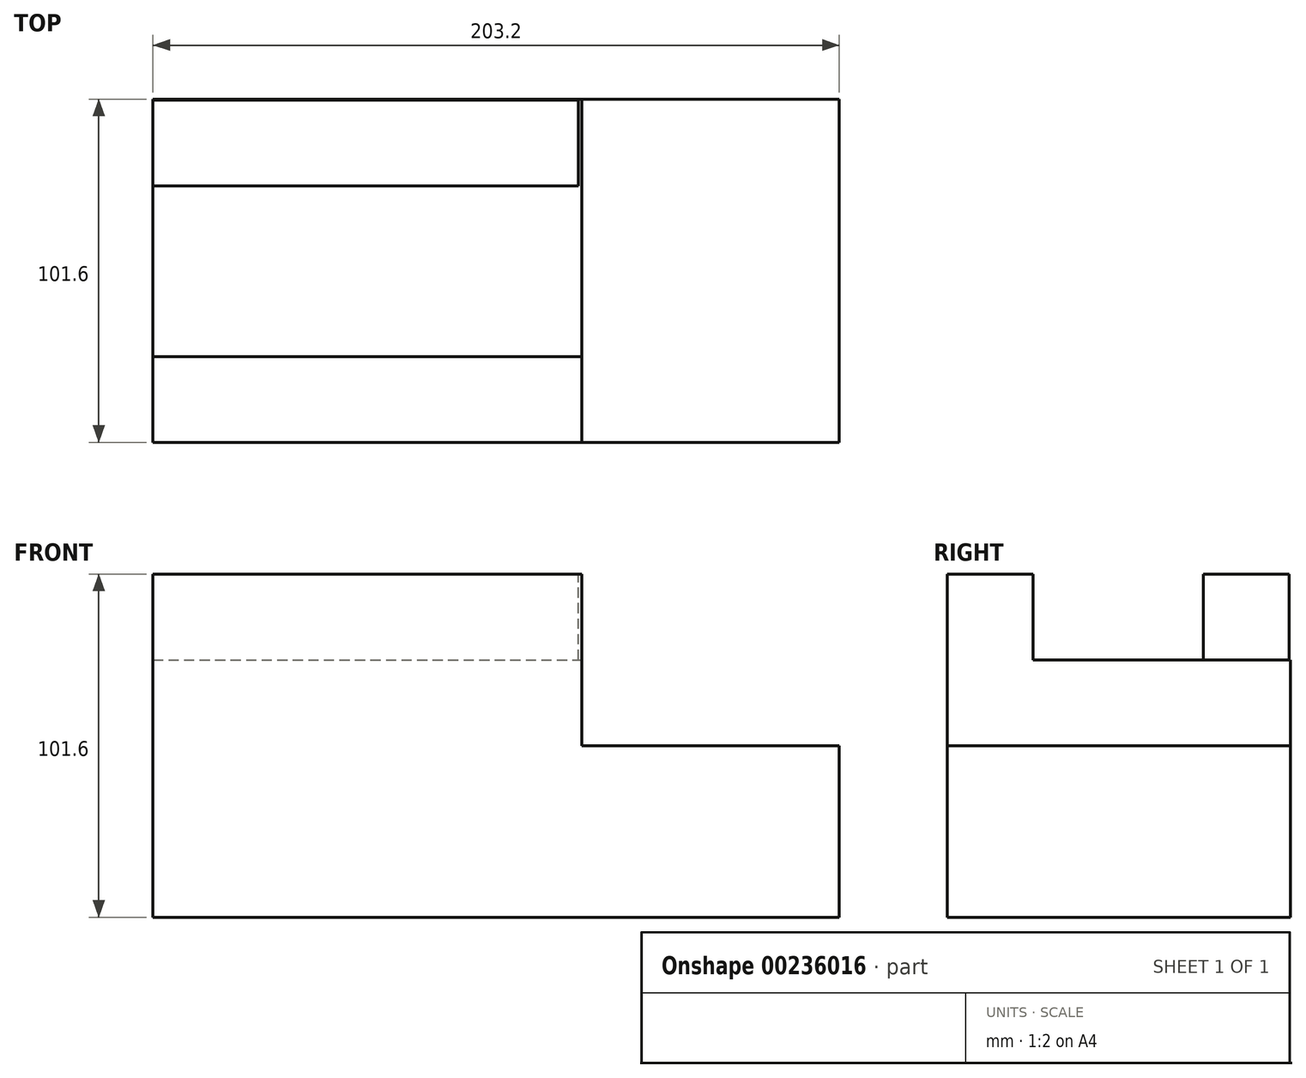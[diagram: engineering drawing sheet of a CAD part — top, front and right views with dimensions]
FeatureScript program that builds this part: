
annotation { "Feature Type Name" : "Feature", "Feature Type Description" : "" }
export const myFeature = defineFeature(function(context is Context, id is Id, definition is map)
    precondition{}
    {
        {
            var Q0;
            Q0=qCreatedBy(makeId("Top.planeOp"),FACE);
            var sketch = newSketch(context, id + "F0", { "sketchPlane" : qUnion([Q0])});
            skLineSegment(sketch, "E0.bottom", {"start": v(-140.96, -30.87) * mm, "end": v(62.24, -30.87) * mm});
            skLineSegment(sketch, "E0.top", {"start": v(-140.96, 70.73) * mm, "end": v(62.24, 70.73) * mm});
            skLineSegment(sketch, "E0.left", {"start": v(-140.96, -30.87) * mm, "end": v(-140.96, 70.73) * mm});
            skLineSegment(sketch, "E0.right", {"start": v(62.24, -30.87) * mm, "end": v(62.24, 70.73) * mm});
            skSolve(sketch);
        }
        {
            var Q0;
            Q0=makeQuery(id+"F0.imprint","IMPRINT",FACE,{"disambiguationData":[TD([[makeQuery(id+"F0.imprint","IMPRINT",EDGE,{"derivedFrom":sQuery(id+"F0.wireOp",EDGE,"E0.bottom")}),1.0]])]});
            extrude(context, id + "F1", {"entities" : qUnion([Q0]), "depth" : 101.6 * mm});
        }
        {
            var Q0;
            Q0=makeQuery(id+"F1.opExtrude","CAP_FACE",FACE,{"disambiguationData":[OSD([sQuery(id+"F0.wireOp",EDGE,"E0.bottom"),sQuery(id+"F0.wireOp",EDGE,"E0.top"),sQuery(id+"F0.wireOp",EDGE,"E0.left"),sQuery(id+"F0.wireOp",EDGE,"E0.right")])],"isStart":false});
            var sketch = newSketch(context, id + "F2", { "sketchPlane" : qUnion([Q0])});
            skLineSegment(sketch, "E1.bottom", {"start": v(-13.96, -30.87) * mm, "end": v(62.24, -30.87) * mm});
            skLineSegment(sketch, "E1.top", {"start": v(-13.96, 70.73) * mm, "end": v(62.24, 70.73) * mm});
            skLineSegment(sketch, "E1.left", {"start": v(-13.96, -30.87) * mm, "end": v(-13.96, 70.73) * mm});
            skLineSegment(sketch, "E1.right", {"start": v(62.24, -30.87) * mm, "end": v(62.24, 70.73) * mm});
            skSolve(sketch);
        }
        {
            var Q0;
            Q0=makeQuery(id+"F2.imprint","IMPRINT",FACE,{"disambiguationData":[TD([[makeQuery(id+"F2.imprint","IMPRINT",EDGE,{"derivedFrom":sQuery(id+"F2.wireOp",EDGE,"E1.bottom")}),1.0]])]});
            extrude(context, id + "F3", {"entities" : qUnion([Q0]), "operationType" : NewBodyOperationType.REMOVE, "oppositeDirection" : true, "depth" : 50.8 * mm});
        }
        {
            var Q0;
            Q0=makeQuery(id+"F1.opExtrude","CAP_FACE",FACE,{"disambiguationData":[OSD([sQuery(id+"F0.wireOp",EDGE,"E0.bottom"),sQuery(id+"F0.wireOp",EDGE,"E0.top"),sQuery(id+"F0.wireOp",EDGE,"E0.left"),sQuery(id+"F0.wireOp",EDGE,"E0.right")])],"isStart":false});
            var sketch = newSketch(context, id + "F4", { "sketchPlane" : qUnion([Q0])});
            skLineSegment(sketch, "E2.bottom", {"start": v(-140.96, -5.47) * mm, "end": v(-13.96, -5.47) * mm});
            skLineSegment(sketch, "E2.top", {"start": v(-140.96, -30.87) * mm, "end": v(-13.96, -30.87) * mm});
            skLineSegment(sketch, "E2.left", {"start": v(-140.96, -5.47) * mm, "end": v(-140.96, -30.87) * mm});
            skLineSegment(sketch, "E2.right", {"start": v(-13.96, -5.47) * mm, "end": v(-13.96, -30.87) * mm});
            skSolve(sketch);
        }
        {
            var Q0;
            {var subQ0=sQuery(id+"F4.wireOp",EDGE,"E2.bottom");Q0=makeQuery(id+"F4.imprint","IMPRINT",FACE,{"disambiguationData":[TD([[makeQuery(id+"F4.imprint","IMPRINT",EDGE,{"derivedFrom":subQ0}),1.0]])]});}
            var sketch = newSketch(context, id + "F5", { "sketchPlane" : qUnion([Q0])});
            skLineSegment(sketch, "E3.bottom", {"start": v(-142.06, 70.36) * mm, "end": v(-15.06, 70.36) * mm});
            skLineSegment(sketch, "E3.top", {"start": v(-142.06, 44.96) * mm, "end": v(-15.06, 44.96) * mm});
            skLineSegment(sketch, "E3.left", {"start": v(-142.06, 70.36) * mm, "end": v(-142.06, 44.96) * mm});
            skLineSegment(sketch, "E3.right", {"start": v(-15.06, 70.36) * mm, "end": v(-15.06, 44.96) * mm});
            skSolve(sketch);
        }
        {
            var Q0;
            {var subQ2=sQuery(id+"F5.wireOp",EDGE,"E3.right");Q0=makeQuery(id+"F5.imprint","IMPRINT",FACE,{"disambiguationData":[TD([[makeQuery(id+"F5.imprint","IMPRINT",EDGE,{"derivedFrom":subQ2}),1.0]])]});}
            extrude(context, id + "F6", {"entities" : qUnion([Q0]), "operationType" : NewBodyOperationType.REMOVE, "oppositeDirection" : true, "depth" : 25.4 * mm});
        }
    });
